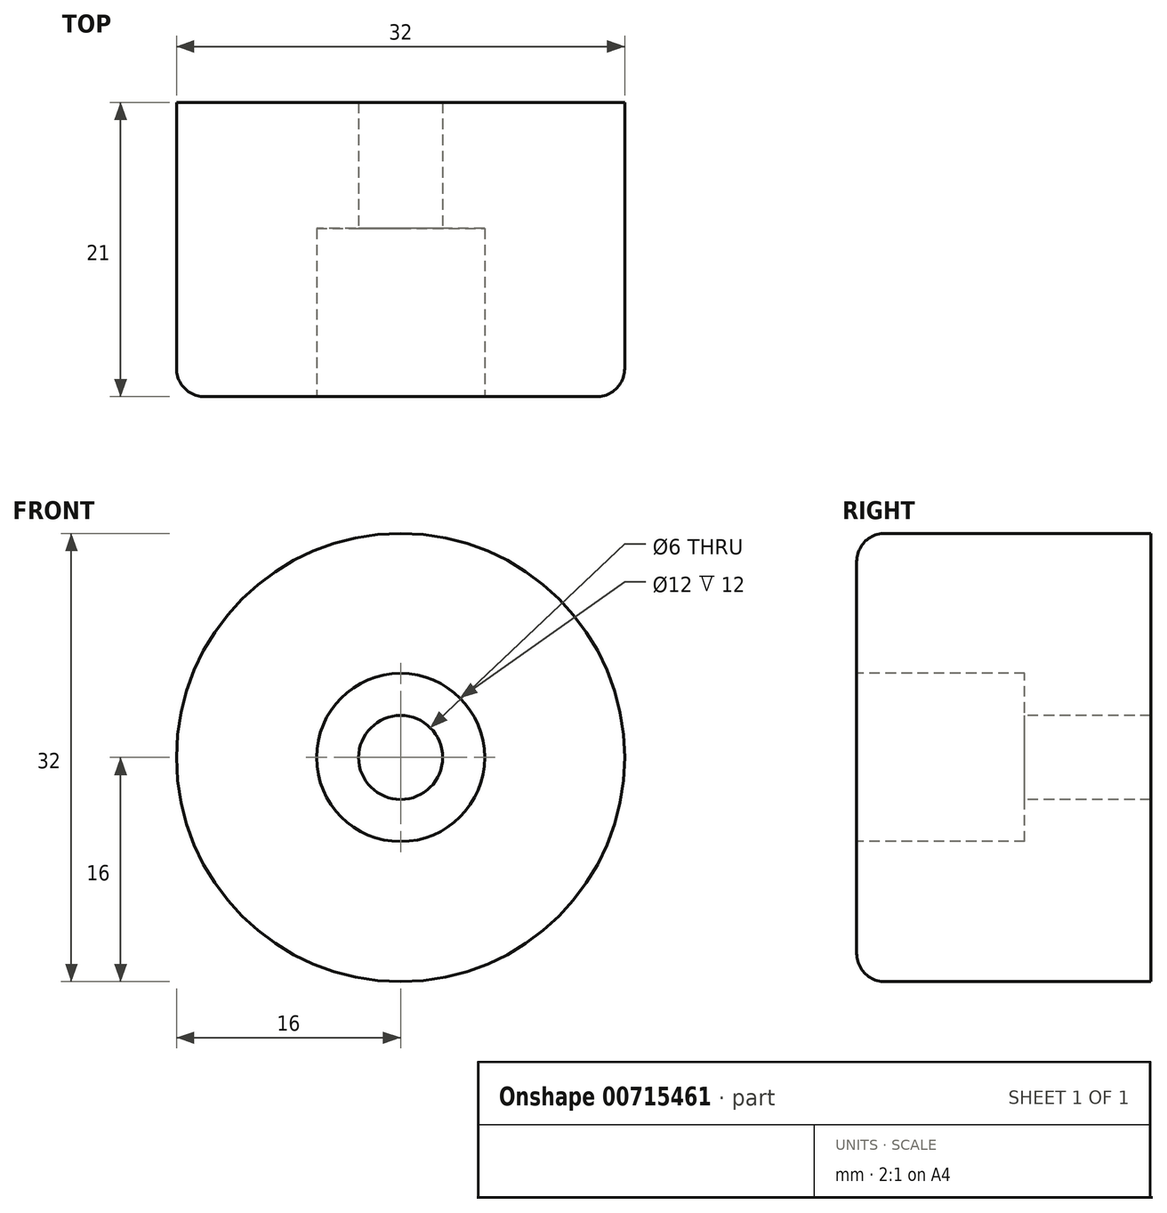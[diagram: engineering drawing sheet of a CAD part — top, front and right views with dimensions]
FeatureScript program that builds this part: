
annotation { "Feature Type Name" : "Feature", "Feature Type Description" : "" }
export const myFeature = defineFeature(function(context is Context, id is Id, definition is map)
    precondition{}
    {
        {
            var Q0;
            Q0=qCreatedBy(makeId("Front.planeOp"),FACE);
            var sketch = newSketch(context, id + "F0", { "sketchPlane" : qUnion([Q0])});
            skCircle(sketch, "E0", {"center": v(0, 0) * mm, "radius": 16 * mm});
            skSolve(sketch);
        }
        {
            var Q0;
            Q0 = qSketchRegion(id + "F0", true);
            extrude(context, id + "F1", {"entities" : qUnion([Q0]), "depth" : 21 * mm, "offsetDistance" : 25 * mm});
        }
        {
            var Q0;
            Q0=makeQuery(id+"F1.opExtrude","CAP_FACE",FACE,{"disambiguationData":[OSD([sQuery(id+"F0.wireOp",EDGE,"E0")])],"isStart":false});
            var sketch = newSketch(context, id + "F2", { "sketchPlane" : qUnion([Q0])});
            skLineSegment(sketch, "E1", {"start": v(0, -16) * mm, "end": v(0, 16) * mm, "construction": true});
            skLineSegment(sketch, "E2", {"start": v(-16, 0) * mm, "end": v(16, 0) * mm, "construction": true});
            skPoint(sketch, "E3", {"position": v(0, 0) * mm});
            skSolve(sketch);
        }
        {
            var Q0;
            Q0=sQuery(id+"F2.wireOp",VERTEX,"E3");
            var Q1;
            Q1=makeQuery(id+"F1.opExtrude","SWEPT_BODY",BODY,{"disambiguationData":[OSD([sQuery(id+"F0.wireOp",EDGE,"E0")])]});
            hole(context, id + "F3", {"style" : HoleStyle.C_BORE, "endStyle" : HoleEndStyle.BLIND, "standardTappedOrClearance" : lookupTablePath({ "standard" : "ISO", "size" : "6", "type" : "Drilled" }), "standardBlindInLast" : lookupTablePath({ "standard" : "ISO", "size" : "6", "type" : "Drilled" }), "holeDiameter" : 6 * mm, "cBoreDiameter" : 12 * mm, "cBoreDepth" : 12 * mm, "majorDiameter" : 6 * mm, "holeDepth" : 21 * mm, "isTappedThrough" : true, "tappedDepth" : 12 * mm, "tapClearance" : 3, "locations" : qUnion([Q0]), "scope" : qUnion([Q1])});
        }
        {
            var Q0;
            Q0=makeQuery(id+"F1.opExtrude","CAP_EDGE",EDGE,{"disambiguationData":[OSD([sQuery(id+"F0.wireOp",EDGE,"E0")])],"isStart":false});
            fillet(context, id + "F4", {"entities" : qUnion([Q0]), "radius" : 2 * mm, "tangentPropagation" : true, "allowEdgeOverflow" : false});
        }
    });
